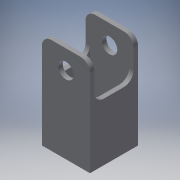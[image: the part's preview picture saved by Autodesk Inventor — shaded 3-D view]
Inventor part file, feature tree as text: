
AUTODESK INVENTOR PART (.ipt)
format: ipt  version: 2018 (Build 220112000, 112)  size: 144,896 bytes
history: native  units: mm
features: extrude x3, sketch x3, other x1, shell x1, fillet x1
ambient origin geometry x8: Origin, YZ Plane, XZ Plane, XY Plane, X Axis, Y Axis, Z Axis, Center Point
bodies: Body1 (feature_tree)
feature tree (9):
  other  "ソリッド1"
  extrude  "押し出し1"  Depth=25.0mm
  shell  "シェル1"  Thickness=25.0mm
  extrude  "押し出し2"  Depth=50.0mm TaperAngle=0.0deg
  extrude  "押し出し3"  Depth=2.3mm
  fillet  "フィレット1"  Radius=20.0mm
  sketch  "スケッチ1"
  sketch  "スケッチ2"
  sketch  "スケッチ3"
